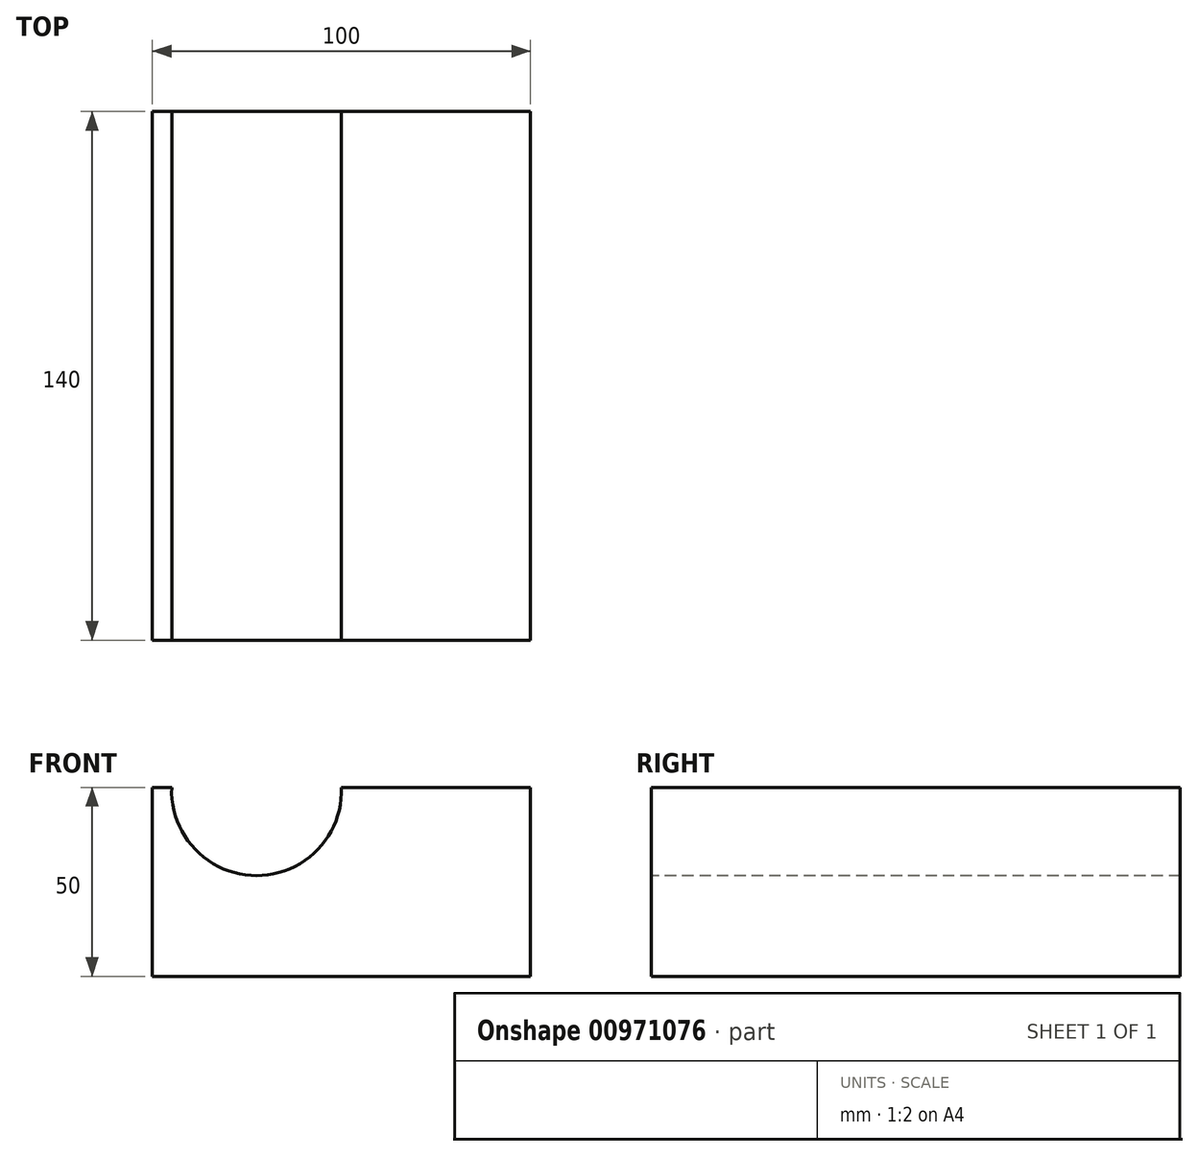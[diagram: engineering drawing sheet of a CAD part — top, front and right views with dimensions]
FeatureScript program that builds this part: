
annotation { "Feature Type Name" : "Feature", "Feature Type Description" : "" }
export const myFeature = defineFeature(function(context is Context, id is Id, definition is map)
    precondition{}
    {
        {
            var Q0;
            Q0=qCreatedBy(makeId("Front.planeOp"),FACE);
            var sketch = newSketch(context, id + "F0", { "sketchPlane" : qUnion([Q0])});
            skLineSegment(sketch, "E0.bottom", {"start": v(-50.35, 24.59) * mm, "end": v(49.65, 24.59) * mm});
            skLineSegment(sketch, "E0.top", {"start": v(-50.35, -25.41) * mm, "end": v(49.65, -25.41) * mm});
            skLineSegment(sketch, "E0.left", {"start": v(-50.35, 24.59) * mm, "end": v(-50.35, -25.41) * mm});
            skLineSegment(sketch, "E0.right", {"start": v(49.65, 24.59) * mm, "end": v(49.65, -25.41) * mm});
            skLineSegment(sketch, "E1", {"start": v(-50.35, 24.59) * mm, "end": v(-0.35, 24.59) * mm});
            skArc(sketch, "E2", {"start": v(-45.27, 24.59) * mm, "mid": v(-22.81, 1.26) * mm, "end": v(-0.35, 24.59) * mm});
            skLineSegment(sketch, "E3", {"start": v(-45.27, 24.59) * mm, "end": v(-0.35, 24.59) * mm});
            skSolve(sketch);
        }
        {
            var Q0;
            Q0=makeQuery(id+"F0.imprint","IMPRINT",FACE,{"disambiguationData":[TD([[makeQuery(id+"F0.imprint","IMPRINT",EDGE,{"derivedFrom":sQuery(id+"F0.wireOp",EDGE,"E0.bottom")}),-1.0]])]});
            extrude(context, id + "F1", {"entities" : qUnion([Q0]), "depth" : -140 * mm, "offsetDistance" : 25 * mm});
        }
    });
